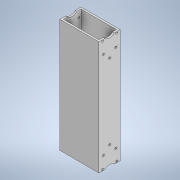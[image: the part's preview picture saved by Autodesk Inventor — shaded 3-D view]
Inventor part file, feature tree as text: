
AUTODESK INVENTOR PART (.ipt)
format: ipt  version: 2022 (Build 260153000, 153)  size: 228,352 bytes
history: native  units: mm
features: other x15, sketch x7, extrude x6, projected_geometry x3, mirror x1, loft x1, pattern_circular x1
ambient origin geometry x8: Origin, YZ Plane, XZ Plane, XY Plane, X Axis, Y Axis, Z Axis, Center Point
bodies: Body1 (feature_tree)
feature tree (34):
  other  "Твердое тело1"
  extrude  "Выдавливание1"  Depth=40.2mm
  extrude  "Выдавливание3"  Depth=20.0mm
  extrude  "Выдавливание4"  Depth=2.0mm
  extrude  "Выдавливание2"  Depth=2.0mm
  other  "РабПлоскость3"
  extrude  "Выдавливание5"  Depth=24.75mm TaperAngle=0.0deg
  other  "РабПлоскость5"
  mirror  "Зеркальное отражение2"
  extrude  "Выдавливание6"  Depth=2.0mm TaperAngle=0.0deg
  other  "РабПлоскость1"
  loft  "Лофт1"
  other  "РабОсь6"
  other  "РабПлоскость4"
  other  "РабТочка2"
  other  "РабОсь10"
  pattern_circular  "Круговой массив1"  [2 undecoded]
  sketch  "Эскиз2"
  sketch  "Эскиз3"
  sketch  "Эскиз4"
  projected_geometry  "Спроецированная петля1"
  sketch  "Эскиз5"
  projected_geometry  "Спроецированная петля2"
  sketch  "Эскиз6"
  other  "Ребра1"
  other  "РабОсь4"
  other  "РабОсь5"
  other  "РабТочка1"
  other  "РабОсь7"
  other  "РабОсь9"
  other  "РабТочка3"
  sketch  "Эскиз7"
  sketch  "Эскиз9"
  projected_geometry  "Спроецированная петля3"
note: 2 required parameter values undecoded (feature->parameter linkage not recoverable at this tier; creation-order binding heuristic only, values carry confidence <= 0.55)
